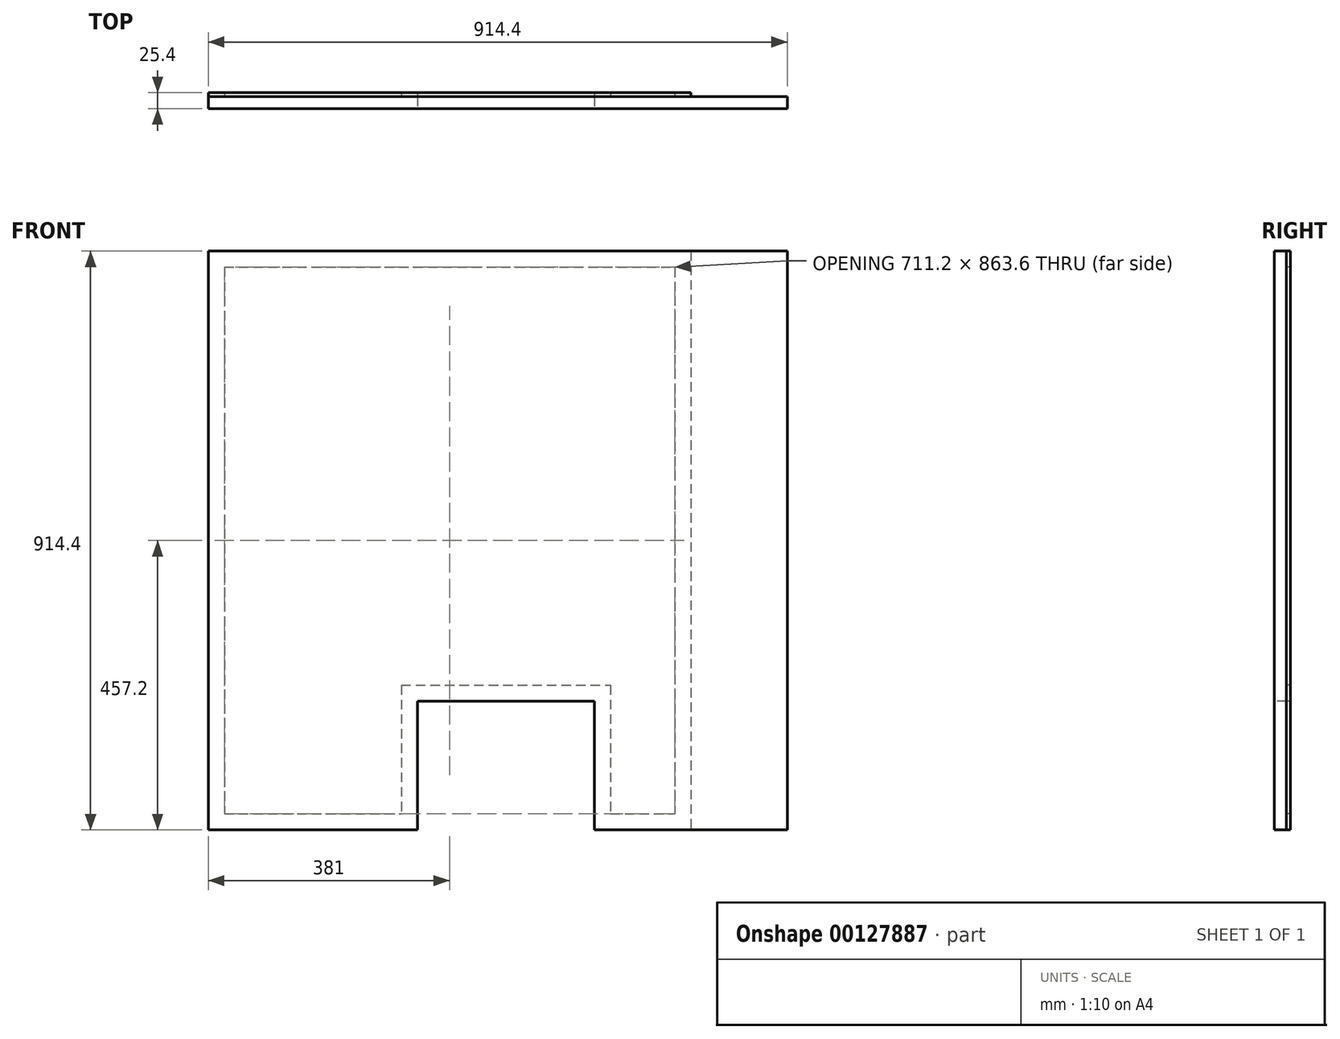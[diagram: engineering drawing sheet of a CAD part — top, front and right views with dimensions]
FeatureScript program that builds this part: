
annotation { "Feature Type Name" : "Feature", "Feature Type Description" : "" }
export const myFeature = defineFeature(function(context is Context, id is Id, definition is map)
    precondition{}
    {
        {
            var Q0;
            Q0=qCreatedBy(makeId("Front.planeOp"),FACE);
            var sketch = newSketch(context, id + "F3", { "sketchPlane" : qUnion([Q0])});
            skLineSegment(sketch, "E0.bottom", {"start": v(457.2, 457.2) * mm, "end": v(-457.2, 457.2) * mm});
            skLineSegment(sketch, "E0.top", {"start": v(457.2, -457.2) * mm, "end": v(-457.2, -457.2) * mm});
            skLineSegment(sketch, "E0.left", {"start": v(457.2, 457.2) * mm, "end": v(457.2, -457.2) * mm});
            skLineSegment(sketch, "E0.right", {"start": v(-457.2, 457.2) * mm, "end": v(-457.2, -457.2) * mm});
            skPoint(sketch, "E0.middle", {"position": v(0, 0) * mm});
            skSolve(sketch);
        }
        {
            var Q0;
            Q0=makeQuery(id+"F3.imprint","IMPRINT",FACE,{"disambiguationData":[TD([[makeQuery(id+"F3.imprint","IMPRINT",EDGE,{"derivedFrom":sQuery(id+"F3.wireOp",EDGE,"E0.bottom")}),1.0]])]});
            extrude(context, id + "F4", {"entities" : qUnion([Q0]), "depth" : 19.05 * mm});
        }
        {
            var Q0;
            Q0=makeQuery(id+"F4.opExtrude","CAP_FACE",FACE,{"disambiguationData":[OSD([sQuery(id+"F3.wireOp",EDGE,"E0.bottom"),sQuery(id+"F3.wireOp",EDGE,"E0.top"),sQuery(id+"F3.wireOp",EDGE,"E0.left"),sQuery(id+"F3.wireOp",EDGE,"E0.right")])],"isStart":false});
            var sketch = newSketch(context, id + "F0", { "sketchPlane" : qUnion([Q0])});
            skLineSegment(sketch, "E1.bottom", {"start": v(-127, -254) * mm, "end": v(152.4, -254) * mm});
            skLineSegment(sketch, "E1.top", {"start": v(-127, -457.2) * mm, "end": v(152.4, -457.2) * mm});
            skLineSegment(sketch, "E1.left", {"start": v(152.4, -254) * mm, "end": v(152.4, -457.2) * mm});
            skLineSegment(sketch, "E1.right", {"start": v(-127, -254) * mm, "end": v(-127, -457.2) * mm});
            skSolve(sketch);
        }
        {
            var Q0;
            Q0=makeQuery(id+"F0.imprint","IMPRINT",FACE,{"disambiguationData":[TD([[makeQuery(id+"F0.imprint","IMPRINT",EDGE,{"derivedFrom":sQuery(id+"F0.wireOp",EDGE,"E1.bottom")}),-1.0]])]});
            extrude(context, id + "F5", {"entities" : qUnion([Q0]), "operationType" : NewBodyOperationType.REMOVE, "oppositeDirection" : true, "depth" : 25 * mm});
        }
        {
            var Q0;
            Q0=makeQuery(id+"F4.opExtrude","CAP_FACE",FACE,{"disambiguationData":[OSD([sQuery(id+"F3.wireOp",EDGE,"E0.bottom"),sQuery(id+"F3.wireOp",EDGE,"E0.top"),sQuery(id+"F3.wireOp",EDGE,"E0.left"),sQuery(id+"F3.wireOp",EDGE,"E0.right")])],"isStart":true});
            var sketch = newSketch(context, id + "F1", { "sketchPlane" : qUnion([Q0])});
            skLineSegment(sketch, "E2", {"start": v(76.2, 457.2) * mm, "end": v(76.2, -457.2) * mm, "construction": true});
            skLineSegment(sketch, "E3", {"start": v(457.2, 0) * mm, "end": v(-304.8, 0) * mm, "construction": true});
            skPoint(sketch, "E3.endSnap0", {"position": v(76.2, 0) * mm});
            skLineSegment(sketch, "E4.bottom", {"start": v(457.2, 457.2) * mm, "end": v(-304.8, 457.2) * mm});
            skLineSegment(sketch, "E4.top", {"start": v(457.2, -457.2) * mm, "end": v(-304.8, -457.2) * mm});
            skLineSegment(sketch, "E4.left", {"start": v(457.2, 457.2) * mm, "end": v(457.2, -457.2) * mm});
            skLineSegment(sketch, "E4.right", {"start": v(-304.8, 457.2) * mm, "end": v(-304.8, -457.2) * mm});
            skLineSegment(sketch, "E5.0", {"start": v(431.8, 431.8) * mm, "end": v(-279.4, 431.8) * mm});
            skLineSegment(sketch, "E5.1", {"start": v(431.8, 431.8) * mm, "end": v(431.8, -431.8) * mm});
            skLineSegment(sketch, "E5.2", {"start": v(431.8, -431.8) * mm, "end": v(-279.4, -431.8) * mm});
            skLineSegment(sketch, "E5.3", {"start": v(-279.4, 431.8) * mm, "end": v(-279.4, -431.8) * mm});
            skLineSegment(sketch, "E6.0", {"start": v(-152.4, -254) * mm, "end": v(-152.4, -457.2) * mm});
            skLineSegment(sketch, "E6.1", {"start": v(127, -254) * mm, "end": v(-152.4, -254) * mm});
            skLineSegment(sketch, "E6.2", {"start": v(127, -254) * mm, "end": v(127, -457.2) * mm});
            skLineSegment(sketch, "E7.0", {"start": v(-177.8, -228.6) * mm, "end": v(-177.8, -457.2) * mm});
            skLineSegment(sketch, "E7.1", {"start": v(152.4, -228.6) * mm, "end": v(-177.8, -228.6) * mm});
            skLineSegment(sketch, "E7.2", {"start": v(152.4, -228.6) * mm, "end": v(152.4, -457.2) * mm});
            skSolve(sketch);
        }
        {
            var Q0;
            Q0=makeQuery(id+"F1.imprint","IMPRINT",FACE,{"disambiguationData":[TD([[makeQuery(id+"F1.imprint","IMPRINT",EDGE,{"derivedFrom":sQuery(id+"F1.wireOp",EDGE,"E4.bottom")}),-1.0]])]});
            var Q1;
            {var subQ0=sQuery(id+"F1.wireOp",EDGE,"E6.0");var subQ1=sQuery(id+"F1.wireOp",EDGE,"E4.top");var subQ2=makeQuery(id+"F1.imprint","INTERSECT",VERTEX,{"derivedFrom":[subQ1,subQ0]});var subQ3=sQuery(id+"F1.wireOp",EDGE,"E7.0");var subQ4=makeQuery(id+"F1.imprint","INTERSECT",VERTEX,{"derivedFrom":[subQ1,subQ3]});Q1=makeQuery(id+"F1.imprint","IMPRINT",FACE,{"disambiguationData":[TD([[makeQuery(id+"F1.imprint","IMPRINT",EDGE,{"disambiguationData":[TD([[subQ2,1.0],[subQ4,-1.0]])],"derivedFrom":subQ1}),1.0]])]});}
            var Q2;
            {var subQ0=sQuery(id+"F1.wireOp",EDGE,"E6.1");Q2=makeQuery(id+"F1.imprint","IMPRINT",FACE,{"disambiguationData":[TD([[makeQuery(id+"F1.imprint","IMPRINT",EDGE,{"derivedFrom":subQ0}),-1.0]])]});}
            var Q3;
            {var subQ0=sQuery(id+"F1.wireOp",EDGE,"E6.2");var subQ1=sQuery(id+"F1.wireOp",EDGE,"E4.top");var subQ2=makeQuery(id+"F1.imprint","INTERSECT",VERTEX,{"derivedFrom":[subQ1,subQ0]});var subQ3=sQuery(id+"F1.wireOp",EDGE,"E7.2");var subQ4=makeQuery(id+"F1.imprint","INTERSECT",VERTEX,{"derivedFrom":[subQ1,subQ3]});Q3=makeQuery(id+"F1.imprint","IMPRINT",FACE,{"disambiguationData":[TD([[makeQuery(id+"F1.imprint","IMPRINT",EDGE,{"disambiguationData":[TD([[subQ2,-1.0],[subQ4,1.0]])],"derivedFrom":subQ1}),1.0]])]});}
            extrude(context, id + "F2", {"entities" : qUnion([Q0, Q1, Q2, Q3]), "depth" : 6.35 * mm});
        }
    });
